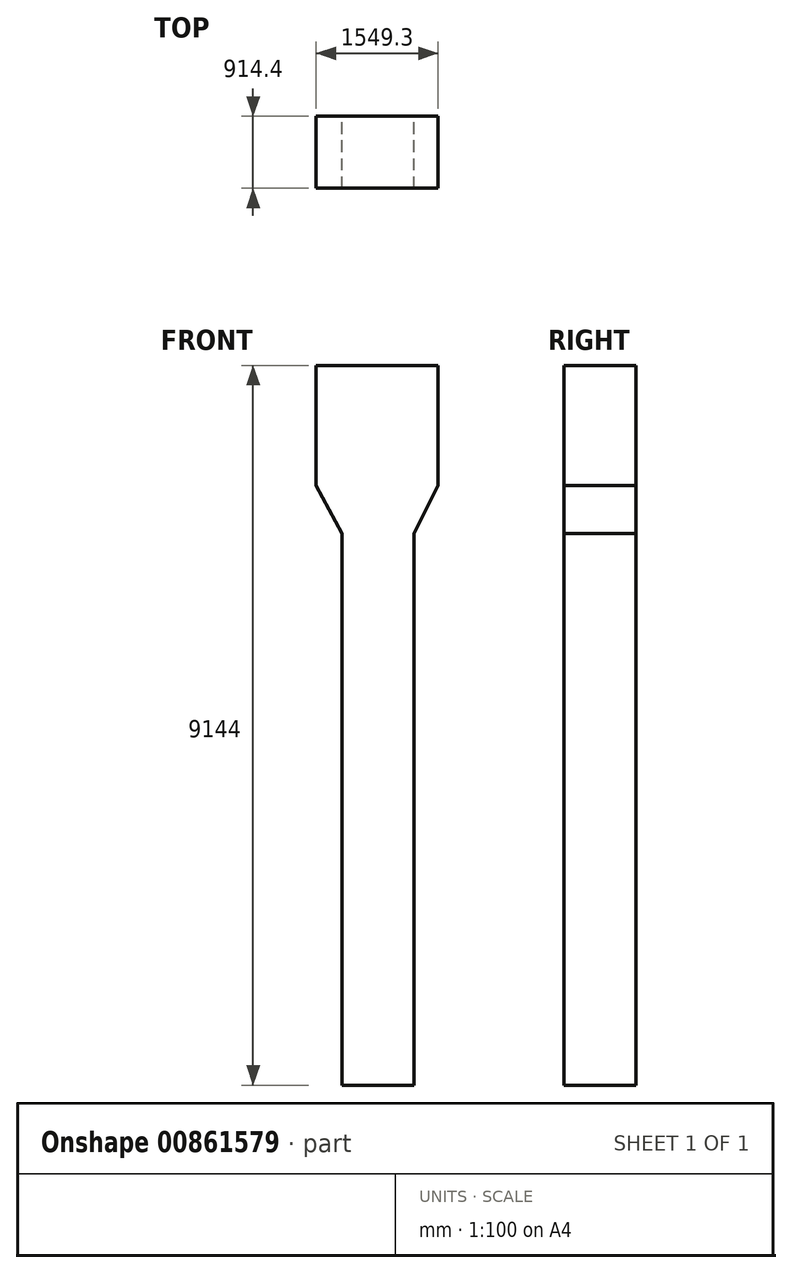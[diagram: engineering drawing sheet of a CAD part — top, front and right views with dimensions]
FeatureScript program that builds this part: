
annotation { "Feature Type Name" : "Feature", "Feature Type Description" : "" }
export const myFeature = defineFeature(function(context is Context, id is Id, definition is map)
    precondition{}
    {
        {
            var Q0;
            Q0=qCreatedBy(makeId("Front.planeOp"),FACE);
            var sketch = newSketch(context, id + "F0", { "sketchPlane" : qUnion([Q0])});
            skLineSegment(sketch, "E0.bottom", {"start": v(774.65, 4572) * mm, "end": v(-774.65, 4572) * mm, "construction": true});
            skLineSegment(sketch, "E0.top", {"start": v(774.65, -4572) * mm, "end": v(-774.65, -4572) * mm, "construction": true});
            skLineSegment(sketch, "E0.left", {"start": v(774.65, 4572) * mm, "end": v(774.65, -4572) * mm, "construction": true});
            skLineSegment(sketch, "E0.right", {"start": v(-774.65, 4572) * mm, "end": v(-774.65, -4572) * mm, "construction": true});
            skPoint(sketch, "E0.middle", {"position": v(0, 0) * mm});
            skLineSegment(sketch, "E1.bottom", {"start": v(-774.65, 4572) * mm, "end": v(774.65, 4572) * mm});
            skLineSegment(sketch, "E1.top", {"start": v(-774.65, 3048) * mm, "end": v(774.65, 3048) * mm});
            skLineSegment(sketch, "E1.left", {"start": v(-774.65, 4572) * mm, "end": v(-774.65, 3048) * mm});
            skLineSegment(sketch, "E1.right", {"start": v(774.65, 4572) * mm, "end": v(774.65, 3048) * mm});
            skLineSegment(sketch, "E2.bottom", {"start": v(-444.55, -4572) * mm, "end": v(469.85, -4572) * mm, "construction": true});
            skLineSegment(sketch, "E2.top", {"start": v(-444.55, 3048) * mm, "end": v(469.85, 3048) * mm, "construction": true});
            skLineSegment(sketch, "E2.left", {"start": v(-444.55, -4572) * mm, "end": v(-444.55, 3048) * mm, "construction": true});
            skLineSegment(sketch, "E2.right", {"start": v(469.85, -4572) * mm, "end": v(469.85, 3048) * mm, "construction": true});
            skLineSegment(sketch, "E3", {"start": v(-774.65, 2438.4) * mm, "end": v(774.65, 2438.4) * mm, "construction": true});
            skLineSegment(sketch, "E4", {"start": v(-774.65, 3048) * mm, "end": v(-444.55, 2438.4) * mm});
            skLineSegment(sketch, "E5", {"start": v(-444.55, 2438.4) * mm, "end": v(-444.55, -4572) * mm});
            skLineSegment(sketch, "E6", {"start": v(469.85, -4572) * mm, "end": v(469.85, 2438.4) * mm});
            skLineSegment(sketch, "E7", {"start": v(469.85, 2438.4) * mm, "end": v(774.65, 3048) * mm});
            skLineSegment(sketch, "E8", {"start": v(-444.55, -4572) * mm, "end": v(469.85, -4572) * mm});
            skSolve(sketch);
        }
        {
            var Q0;
            Q0 = qSketchRegion(id + "F0", true);
            extrude(context, id + "F1", {"entities" : qUnion([Q0]), "depth" : 914.4 * mm, "offsetDistance" : 30.48 * mm});
        }
    });
